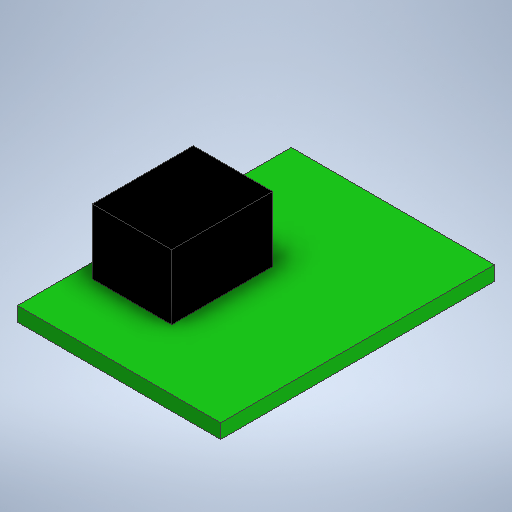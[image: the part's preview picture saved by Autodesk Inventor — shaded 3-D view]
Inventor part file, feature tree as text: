
AUTODESK INVENTOR PART (.ipt)
format: ipt  version: 2025.2 (Build 292293000, 293)  size: 239,104 bytes
history: native  units: mm
features: extrude x2, sketch x2
ambient origin geometry x8: Origin, YZ Plane, XZ Plane, XY Plane, X Axis, Y Axis, Z Axis, Center Point
bodies: Solid1 (feature_tree)
feature tree (4):
  extrude  "Extrusion1"  Depth=19.0mm
  extrude  "Extrusion2"  Depth=5.5mm
  sketch  "Sketch1"  dims[d0=14.1mm d1=19.0mm]
  sketch  "Sketch2"  dims[d2=1.0mm d3=0.0mm d4=5.5mm d5=7.0mm d6=1.0mm d7=4.2mm d8=4.5mm d9=0.0mm]
